# Revit family: 2015_Ventana_Alugom_Matra-135RPT_Corredera-2-Hojas_JGJGJG_xxx
name_source: partatom
category: Ventanas
revit_build: Autodesk Revit 2015 (Build: 20140606_1530(x64)
units: mm (PartAtom-declared; Revit-internal decimal feet)

## types (1)
- 1230x1480 mm Corredera
    AcidificacionAtmosferica = 0
    AcidificacionAtmosfericaPorUnidad = 0
    Acristalamiento = Cristal - Vidrio claro templado
    AguaConsumida = 0
    AguaConsumidaPorUnidad = 0
    Altura = 1480 mm  [stored 4.85564 ft]
    Altura Máxima = 2500 mm  [stored 8.2021 ft]
    Altura Real = 1480 mm  [stored 4.85564 ft]
    Altura de antepecho por defecto = 800 mm  [stored 2.62467 ft]
    AnchoMarco = 147 mm  [stored 0.482283 ft]
    AnchoMarcoCentral = 108 mm  [stored 0.354331 ft]
    Anchura = 1230 mm  [stored 4.03543 ft]
    Anchura Máxima = 4000 mm  [stored 13.1234 ft]
    Anchura Real = 1230 mm  [stored 4.03543 ft]
    Area = 1820400 mm²
    Autor = Bimetica Parametric Design Services, S.L.
    Bimetica = http://www.bimetica.com
    CambioClimatico = 0
    CambioClimaticoPorUnidad = 0
    CerramientoExterior = Sí
    Cierre de muro = Por anfitrión
    Comentarios de tipo = Sistema de Ventana de 2 Hojas Rotura de Puente Térmico Serie Martra 135RPT Corredera
    ConfiguracionPoliamidas = 215600 - 955100
    ControlHumos = No
    Corredera = Sí
    CosteEnergeticoKwh = 0
    CosteEnergeticoMj = 0 J
    CosteMantenimiento = 0
    Descripción = Ventana Corredera
    DesfaseExterior = 0 mm  [stored 0 ft]
    DesfaseInterior = 0 mm  [stored 0 ft]
    DestruccionCapaOzonoEstratosferica = 0
    DestruccionCapaOzonoEstratosfericaPorUnidad = 0
    Detalle Perfileria = Sí
    EmisionCO2 = 0
    EnergiaNoRenovableConsumida = 0
    EnergiaNoRenovableConsumidaPorUnidad = 0
    EnergiaPrimariaTotalConsumida = 0
    EnergiaPrimariaTotalConsumidaPorUnidad = 0
    EnergiaRenovableConsumida = 0
    EnergiaRenovableConsumidaPorUnidad = 0
    EstanqueidadAgua = Clase 8A
    Eutrofizacion = 0
    EutrofizacionPorUnidad = 0
    Fabricante = Grupo ALUGOM
    FactorSolarModificado = 30000000
    FactorSombra = 0
    FaltaDeRecursos = 0
    FaltaDeRecursosPorUnidad = 0
    FechaEmisionElementoBIM = 01/09/2016
    FechaVencimientoElementoBIM = 01/09/2017
    FormacionFotoquimicaOzono = 0
    FormacionFotoquimicaOzonoPorUnidad = 0
    FraccionAreaAcristalamiento = 53.94%
    GrosorAcristalamiento = 22 mm  [stored 0.0721785 ft]
    GrosorMarco = 135 mm  [stored 0.442913 ft]
    IndiceGlobalRedAcusticaTr = 32 dBA
    Manija = Sí
    Marco = Aluminio
    MasaSuperficialKgm2 = 0
    MasterformatCodigo = 08 51 13
    MasterformatTitulo = Aluminum Windows
    MateriaPrima = 0
    Modelo = Serie Martra 135RPT
    Motorizada = No
    OmniclassCodigo = 23.30.20.17.14.14
    OmniclassTitulo = Horizontal Sliding Windows
    Operación = Corredera
    Oscilobatiente = No
    Perimetro = 5420
    PermeabilidadAlAire = Clase 3
    Poliamida = Poliamida, Technoform Bautec, PA66 GF 25
    Practicable = No
    ReferenciaContacto = Alugom
    RepisaExterior = Sí
    RepisaInterior = Sí
    ResiduoInerte = 0
    ResiduoInertePorUnidad = 0
    ResiduoRadioactivo = 0
    ResiduoRadioactivoPorUnidad = 0
    ResiduosNoPeligrosos = 0
    ResiduosNoPeligrososPorUnidad = 0
    ResiduosPeligrosos = 0
    ResiduosPeligrososPorUnidad = 0
    ResistenciaAlViento = Clase C5
    SalidaEmergencia = Sí
    TelefonoContacto = +34 91 616 47 27
    TransmitanciaTermica = 3.7 W/(m²·K)
    UNSPSCCodigo = 30-17-16-07
    UNSPSCTitulo = Horizontal slider windows
    Uniclass2.0Codigo = 30-00-00
    Uniclass2.0Titulo = Accessible openings: Doors and hatches, French windows, sliding wall windows.
    VersionElementoBIM = 1.0
    Y𝑔 P1 = 0.47
    Y𝑔 P2 = 0.47
    a = 3391003.112
    𝐴𝑓 P1 = 710304
    𝐴𝑓 P2 = 128088
    𝐴𝑔 V1 = 491004
    𝐴𝑔 V2 = 491004
    𝑈𝑓 P1 = 2.42
    𝑈𝑓 P2 = 3.039
    𝑈𝑔 V1 = 1
    𝑈𝑔 V2 = 1
    𝑈𝑤 = 1.862779
    𝑙𝑔 P1 = 4028
    𝑙𝑔 P2 = 2372

note: [stored X ft] marks values corroborated as IEEE doubles in the binary element streams (Revit-internal decimal feet)
